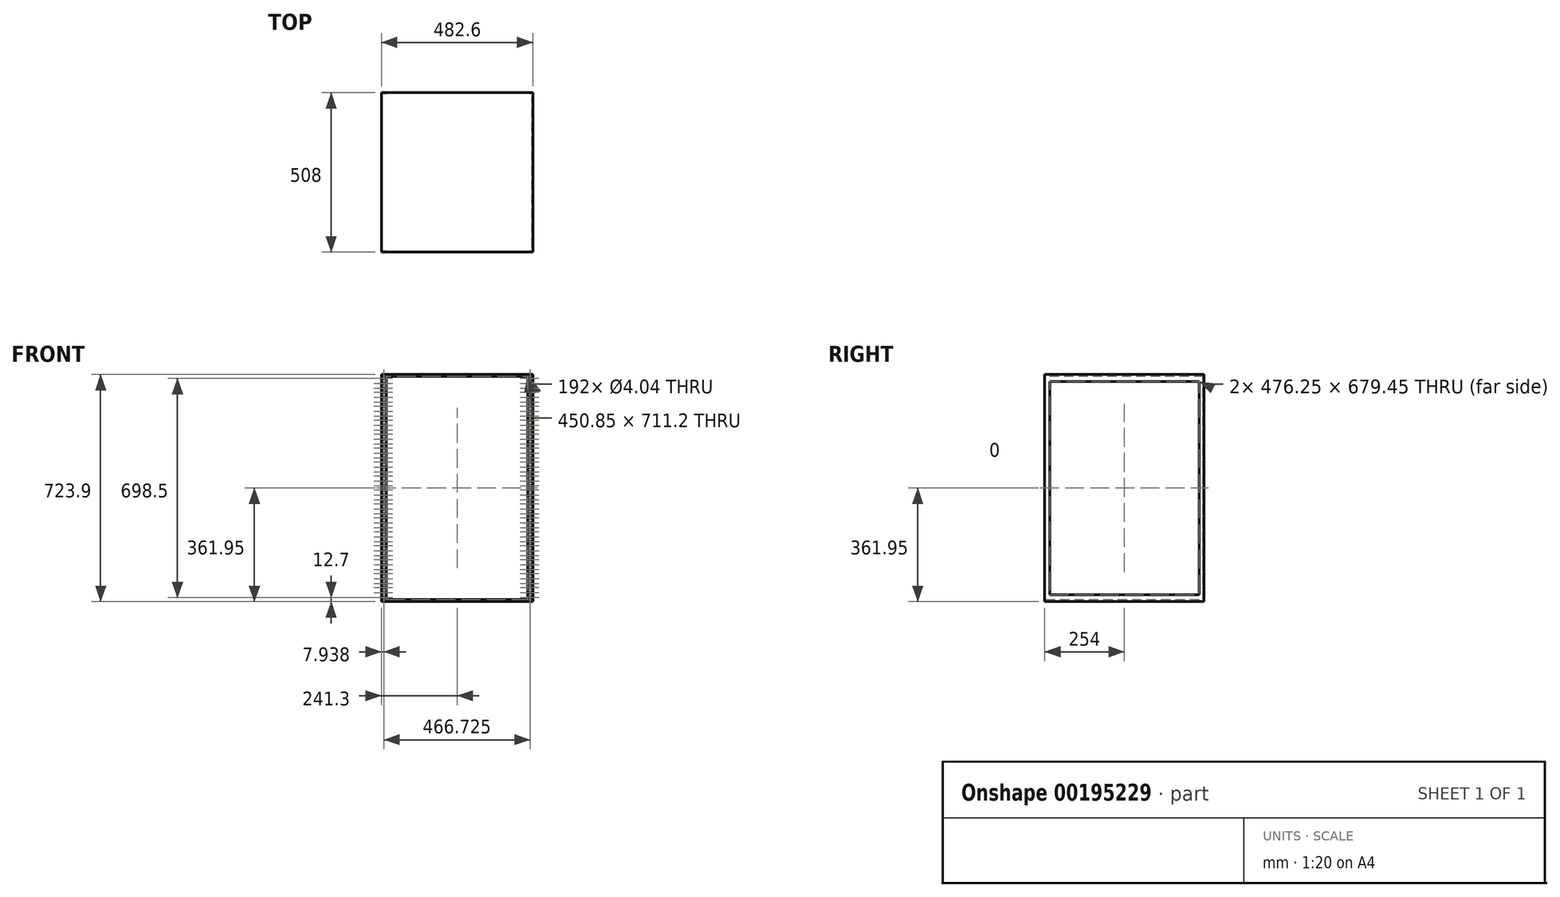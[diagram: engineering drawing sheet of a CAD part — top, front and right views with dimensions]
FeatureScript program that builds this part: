
annotation { "Feature Type Name" : "Feature", "Feature Type Description" : "" }
export const myFeature = defineFeature(function(context is Context, id is Id, definition is map)
    precondition{}
    {
        {
            var Q0;
            Q0=qCreatedBy(makeId("Front.planeOp"),FACE);
            var sketch = newSketch(context, id + "F0", { "sketchPlane" : qUnion([Q0])});
            skLineSegment(sketch, "E0.bottom", {"start": v(-241.3, 355.6) * mm, "end": v(241.3, 355.6) * mm});
            skLineSegment(sketch, "E0.top", {"start": v(-241.3, -355.6) * mm, "end": v(241.3, -355.6) * mm});
            skLineSegment(sketch, "E0.left", {"start": v(-241.3, 355.6) * mm, "end": v(-241.3, -355.6) * mm});
            skLineSegment(sketch, "E0.right", {"start": v(241.3, 355.6) * mm, "end": v(241.3, -355.6) * mm});
            skPoint(sketch, "E0.middle", {"position": v(0, 0) * mm});
            skSolve(sketch);
        }
        {
            var Q0;
            Q0 = qSketchRegion(id + "F0", true);
            extrude(context, id + "F1", {"entities" : qUnion([Q0]), "oppositeDirection" : true, "depth" : 508 * mm});
        }
        {
            var Q0;
            Q0=makeQuery(id+"F1.opExtrude","CAP_FACE",FACE,{"disambiguationData":[OSD([sQuery(id+"F0.wireOp",EDGE,"E0.bottom"),sQuery(id+"F0.wireOp",EDGE,"E0.top"),sQuery(id+"F0.wireOp",EDGE,"E0.left"),sQuery(id+"F0.wireOp",EDGE,"E0.right")])],"isStart":true});
            var sketch = newSketch(context, id + "F2", { "sketchPlane" : qUnion([Q0])});
            skLineSegment(sketch, "E1.bottom", {"start": v(-225.43, 355.6) * mm, "end": v(225.43, 355.6) * mm});
            skLineSegment(sketch, "E1.top", {"start": v(-225.43, -355.6) * mm, "end": v(225.43, -355.6) * mm});
            skLineSegment(sketch, "E1.left", {"start": v(-225.43, 355.6) * mm, "end": v(-225.43, -355.6) * mm});
            skLineSegment(sketch, "E1.right", {"start": v(225.43, 355.6) * mm, "end": v(225.43, -355.6) * mm});
            skPoint(sketch, "E1.middle", {"position": v(0, 0) * mm});
            skSolve(sketch);
        }
        {
            var Q0;
            Q0 = qSketchRegion(id + "F2", true);
            extrude(context, id + "F3", {"entities" : qUnion([Q0]), "operationType" : NewBodyOperationType.REMOVE, "endBound" : BoundingType.THROUGH_ALL, "oppositeDirection" : true, "depth" : 25.4 * mm});
        }
        {
            var Q0;
            Q0=makeQuery(id+"F1.opExtrude","SWEPT_FACE",FACE,{"disambiguationData":[OSD([sQuery(id+"F0.wireOp",EDGE,"E0.left")])]});
            var sketch = newSketch(context, id + "F4", { "sketchPlane" : qUnion([Q0])});
            skLineSegment(sketch, "E2.bottom", {"start": v(-492.13, 339.73) * mm, "end": v(-15.87, 339.73) * mm});
            skLineSegment(sketch, "E2.top", {"start": v(-492.13, -339.73) * mm, "end": v(-15.87, -339.73) * mm});
            skLineSegment(sketch, "E2.left", {"start": v(-492.13, 339.73) * mm, "end": v(-492.13, -339.73) * mm});
            skLineSegment(sketch, "E2.right", {"start": v(-15.88, 339.73) * mm, "end": v(-15.88, -339.73) * mm});
            skPoint(sketch, "E2.middle", {"position": v(-254, 0) * mm});
            skSolve(sketch);
        }
        {
            var Q0;
            Q0 = qSketchRegion(id + "F4", true);
            extrude(context, id + "F5", {"entities" : qUnion([Q0]), "operationType" : NewBodyOperationType.REMOVE, "endBound" : BoundingType.THROUGH_ALL, "oppositeDirection" : true, "depth" : 25.4 * mm});
        }
        {
            var Q0;
            Q0=makeQuery(id+"F1.opExtrude","SWEPT_FACE",FACE,{"disambiguationData":[OSD([sQuery(id+"F0.wireOp",EDGE,"E0.bottom")])]});
            var sketch = newSketch(context, id + "F6", { "sketchPlane" : qUnion([Q0])});
            skLineSegment(sketch, "E3.bottom", {"start": v(-238.76, 505.46) * mm, "end": v(238.76, 505.46) * mm});
            skLineSegment(sketch, "E3.top", {"start": v(-238.76, 2.54) * mm, "end": v(238.76, 2.54) * mm});
            skLineSegment(sketch, "E3.left", {"start": v(-238.76, 505.46) * mm, "end": v(-238.76, 2.54) * mm});
            skLineSegment(sketch, "E3.right", {"start": v(238.76, 505.46) * mm, "end": v(238.76, 2.54) * mm});
            skPoint(sketch, "E3.middle", {"position": v(0, 254) * mm});
            skSolve(sketch);
        }
        {
            var Q0;
            Q0 = qSketchRegion(id + "F6", true);
            extrude(context, id + "F7", {"entities" : qUnion([Q0]), "operationType" : NewBodyOperationType.REMOVE, "endBound" : BoundingType.THROUGH_ALL, "oppositeDirection" : true, "depth" : 25.4 * mm});
        }
        {
            var Q0;
            Q0=makeQuery(id+"F1.opExtrude","CAP_FACE",FACE,{"disambiguationData":[OSD([sQuery(id+"F0.wireOp",EDGE,"E0.bottom"),sQuery(id+"F0.wireOp",EDGE,"E0.top"),sQuery(id+"F0.wireOp",EDGE,"E0.left"),sQuery(id+"F0.wireOp",EDGE,"E0.right")])],"isStart":true});
            var sketch = newSketch(context, id + "F8", { "sketchPlane" : qUnion([Q0])});
            skPoint(sketch, "E4", {"position": v(-233.36, 349.25) * mm});
            skPoint(sketch, "E5", {"position": v(-233.36, 333.38) * mm});
            skPoint(sketch, "E6", {"position": v(-233.36, 317.5) * mm});
            skPoint(sketch, "E7.0.1.0", {"position": v(-233.36, 273.05) * mm});
            skPoint(sketch, "E7.0.1.1", {"position": v(-233.36, 288.93) * mm});
            skPoint(sketch, "E7.0.1.2", {"position": v(-233.36, 304.8) * mm});
            skPoint(sketch, "E7.0.2.0", {"position": v(-233.36, 228.6) * mm});
            skPoint(sketch, "E7.0.2.1", {"position": v(-233.36, 244.48) * mm});
            skPoint(sketch, "E7.0.2.2", {"position": v(-233.36, 260.35) * mm});
            skPoint(sketch, "E7.0.3.0", {"position": v(-233.36, 184.15) * mm});
            skPoint(sketch, "E7.0.3.1", {"position": v(-233.36, 200.03) * mm});
            skPoint(sketch, "E7.0.3.2", {"position": v(-233.36, 215.9) * mm});
            skPoint(sketch, "E7.0.4.0", {"position": v(-233.36, 139.7) * mm});
            skPoint(sketch, "E7.0.4.1", {"position": v(-233.36, 155.58) * mm});
            skPoint(sketch, "E7.0.4.2", {"position": v(-233.36, 171.45) * mm});
            skPoint(sketch, "E7.0.5.0", {"position": v(-233.36, 95.25) * mm});
            skPoint(sketch, "E7.0.5.1", {"position": v(-233.36, 111.13) * mm});
            skPoint(sketch, "E7.0.5.2", {"position": v(-233.36, 127) * mm});
            skPoint(sketch, "E7.0.6.0", {"position": v(-233.36, 50.8) * mm});
            skPoint(sketch, "E7.0.6.1", {"position": v(-233.36, 66.68) * mm});
            skPoint(sketch, "E7.0.6.2", {"position": v(-233.36, 82.55) * mm});
            skPoint(sketch, "E7.0.7.0", {"position": v(-233.36, 6.35) * mm});
            skPoint(sketch, "E7.0.7.1", {"position": v(-233.36, 22.23) * mm});
            skPoint(sketch, "E7.0.7.2", {"position": v(-233.36, 38.1) * mm});
            skPoint(sketch, "E7.0.8.0", {"position": v(-233.36, -38.1) * mm});
            skPoint(sketch, "E7.0.8.1", {"position": v(-233.36, -22.22) * mm});
            skPoint(sketch, "E7.0.8.2", {"position": v(-233.36, -6.35) * mm});
            skPoint(sketch, "E7.0.9.0", {"position": v(-233.36, -82.55) * mm});
            skPoint(sketch, "E7.0.9.1", {"position": v(-233.36, -66.67) * mm});
            skPoint(sketch, "E7.0.9.2", {"position": v(-233.36, -50.8) * mm});
            skPoint(sketch, "E7.0.10.0", {"position": v(-233.36, -127) * mm});
            skPoint(sketch, "E7.0.10.1", {"position": v(-233.36, -111.12) * mm});
            skPoint(sketch, "E7.0.10.2", {"position": v(-233.36, -95.25) * mm});
            skPoint(sketch, "E7.0.11.0", {"position": v(-233.36, -171.45) * mm});
            skPoint(sketch, "E7.0.11.1", {"position": v(-233.36, -155.57) * mm});
            skPoint(sketch, "E7.0.11.2", {"position": v(-233.36, -139.7) * mm});
            skPoint(sketch, "E7.0.12.0", {"position": v(-233.36, -215.9) * mm});
            skPoint(sketch, "E7.0.12.1", {"position": v(-233.36, -200.02) * mm});
            skPoint(sketch, "E7.0.12.2", {"position": v(-233.36, -184.15) * mm});
            skPoint(sketch, "E7.0.13.0", {"position": v(-233.36, -260.35) * mm});
            skPoint(sketch, "E7.0.13.1", {"position": v(-233.36, -244.47) * mm});
            skPoint(sketch, "E7.0.13.2", {"position": v(-233.36, -228.6) * mm});
            skPoint(sketch, "E7.0.14.0", {"position": v(-233.36, -304.8) * mm});
            skPoint(sketch, "E7.0.14.1", {"position": v(-233.36, -288.92) * mm});
            skPoint(sketch, "E7.0.14.2", {"position": v(-233.36, -273.05) * mm});
            skPoint(sketch, "E7.0.15.0", {"position": v(-233.36, -349.25) * mm});
            skPoint(sketch, "E7.0.15.1", {"position": v(-233.36, -333.37) * mm});
            skPoint(sketch, "E7.0.15.2", {"position": v(-233.36, -317.5) * mm});
            skLineSegment(sketch, "E7.direction1", {"start": v(-233.36, 317.5) * mm, "end": v(233.36, 317.5) * mm, "construction": true});
            skLineSegment(sketch, "E7.direction2", {"start": v(-233.36, 317.5) * mm, "end": v(-233.36, 273.05) * mm, "construction": true});
            skPoint(sketch, "E8.0.1.0", {"position": v(233.36, 317.5) * mm});
            skPoint(sketch, "E8.1.1.0", {"position": v(233.36, 333.38) * mm});
            skPoint(sketch, "E8.2.1.0", {"position": v(233.36, 349.25) * mm});
            skPoint(sketch, "E8.0.1.1", {"position": v(233.36, 273.05) * mm});
            skPoint(sketch, "E8.1.1.1", {"position": v(233.36, 288.93) * mm});
            skPoint(sketch, "E8.2.1.1", {"position": v(233.36, 304.8) * mm});
            skPoint(sketch, "E8.0.1.2", {"position": v(233.36, 228.6) * mm});
            skPoint(sketch, "E8.1.1.2", {"position": v(233.36, 244.48) * mm});
            skPoint(sketch, "E8.2.1.2", {"position": v(233.36, 260.35) * mm});
            skPoint(sketch, "E8.0.1.3", {"position": v(233.36, 184.15) * mm});
            skPoint(sketch, "E8.1.1.3", {"position": v(233.36, 200.03) * mm});
            skPoint(sketch, "E8.2.1.3", {"position": v(233.36, 215.9) * mm});
            skPoint(sketch, "E8.0.1.4", {"position": v(233.36, 139.7) * mm});
            skPoint(sketch, "E8.1.1.4", {"position": v(233.36, 155.58) * mm});
            skPoint(sketch, "E8.2.1.4", {"position": v(233.36, 171.45) * mm});
            skPoint(sketch, "E8.0.1.5", {"position": v(233.36, 95.25) * mm});
            skPoint(sketch, "E8.1.1.5", {"position": v(233.36, 111.13) * mm});
            skPoint(sketch, "E8.2.1.5", {"position": v(233.36, 127) * mm});
            skPoint(sketch, "E8.0.1.6", {"position": v(233.36, 50.8) * mm});
            skPoint(sketch, "E8.1.1.6", {"position": v(233.36, 66.68) * mm});
            skPoint(sketch, "E8.2.1.6", {"position": v(233.36, 82.55) * mm});
            skPoint(sketch, "E8.0.1.7", {"position": v(233.36, 6.35) * mm});
            skPoint(sketch, "E8.1.1.7", {"position": v(233.36, 22.23) * mm});
            skPoint(sketch, "E8.2.1.7", {"position": v(233.36, 38.1) * mm});
            skPoint(sketch, "E8.0.1.8", {"position": v(233.36, -38.1) * mm});
            skPoint(sketch, "E8.1.1.8", {"position": v(233.36, -22.22) * mm});
            skPoint(sketch, "E8.2.1.8", {"position": v(233.36, -6.35) * mm});
            skPoint(sketch, "E8.0.1.9", {"position": v(233.36, -82.55) * mm});
            skPoint(sketch, "E8.1.1.9", {"position": v(233.36, -66.67) * mm});
            skPoint(sketch, "E8.2.1.9", {"position": v(233.36, -50.8) * mm});
            skPoint(sketch, "E8.0.1.10", {"position": v(233.36, -127) * mm});
            skPoint(sketch, "E8.1.1.10", {"position": v(233.36, -111.12) * mm});
            skPoint(sketch, "E8.2.1.10", {"position": v(233.36, -95.25) * mm});
            skPoint(sketch, "E8.0.1.11", {"position": v(233.36, -171.45) * mm});
            skPoint(sketch, "E8.1.1.11", {"position": v(233.36, -155.57) * mm});
            skPoint(sketch, "E8.2.1.11", {"position": v(233.36, -139.7) * mm});
            skPoint(sketch, "E8.0.1.12", {"position": v(233.36, -215.9) * mm});
            skPoint(sketch, "E8.1.1.12", {"position": v(233.36, -200.02) * mm});
            skPoint(sketch, "E8.2.1.12", {"position": v(233.36, -184.15) * mm});
            skPoint(sketch, "E8.0.1.13", {"position": v(233.36, -260.35) * mm});
            skPoint(sketch, "E8.1.1.13", {"position": v(233.36, -244.47) * mm});
            skPoint(sketch, "E8.2.1.13", {"position": v(233.36, -228.6) * mm});
            skPoint(sketch, "E8.0.1.14", {"position": v(233.36, -304.8) * mm});
            skPoint(sketch, "E8.1.1.14", {"position": v(233.36, -288.92) * mm});
            skPoint(sketch, "E8.2.1.14", {"position": v(233.36, -273.05) * mm});
            skPoint(sketch, "E8.0.1.15", {"position": v(233.36, -349.25) * mm});
            skPoint(sketch, "E8.1.1.15", {"position": v(233.36, -333.37) * mm});
            skPoint(sketch, "E8.2.1.15", {"position": v(233.36, -317.5) * mm});
            skSolve(sketch);
        }
        {
            var Q0;
            Q0=sQuery(id+"F8.wireOp",VERTEX,"E7.0.2.2");
            var Q1;
            Q1=sQuery(id+"F8.wireOp",VERTEX,"E8.2.1.13");
            var Q2;
            Q2=sQuery(id+"F8.wireOp",VERTEX,"E8.2.1.10");
            var Q3;
            Q3=sQuery(id+"F8.wireOp",VERTEX,"E8.0.1.13");
            var Q4;
            Q4=sQuery(id+"F8.wireOp",VERTEX,"E8.1.1.2");
            var Q5;
            Q5=sQuery(id+"F8.wireOp",VERTEX,"E8.2.1.7");
            var Q6;
            Q6=sQuery(id+"F8.wireOp",VERTEX,"E8.1.1.3");
            var Q7;
            Q7=sQuery(id+"F8.wireOp",VERTEX,"E8.1.1.0");
            var Q8;
            Q8=sQuery(id+"F8.wireOp",VERTEX,"E8.2.1.5");
            var Q9;
            Q9=sQuery(id+"F8.wireOp",VERTEX,"E7.0.14.0");
            var Q10;
            Q10=sQuery(id+"F8.wireOp",VERTEX,"E7.0.11.0");
            var Q11;
            Q11=sQuery(id+"F8.wireOp",VERTEX,"E7.0.8.2");
            var Q12;
            Q12=sQuery(id+"F8.wireOp",VERTEX,"E7.0.5.2");
            var Q13;
            Q13=sQuery(id+"F8.wireOp",VERTEX,"E8.0.1.14");
            var Q14;
            Q14=sQuery(id+"F8.wireOp",VERTEX,"E7.0.8.0");
            var Q15;
            Q15=sQuery(id+"F8.wireOp",VERTEX,"E8.1.1.13");
            var Q16;
            Q16=sQuery(id+"F8.wireOp",VERTEX,"E8.0.1.8");
            var Q17;
            Q17=sQuery(id+"F8.wireOp",VERTEX,"E8.2.1.2");
            var Q18;
            Q18=sQuery(id+"F8.wireOp",VERTEX,"E8.0.1.6");
            var Q19;
            Q19=sQuery(id+"F8.wireOp",VERTEX,"E8.2.1.3");
            var Q20;
            Q20=sQuery(id+"F8.wireOp",VERTEX,"E8.2.1.0");
            var Q21;
            Q21=sQuery(id+"F8.wireOp",VERTEX,"E7.0.6.0");
            var Q22;
            Q22=sQuery(id+"F8.wireOp",VERTEX,"E7.0.11.1");
            var Q23;
            Q23=sQuery(id+"F8.wireOp",VERTEX,"E8.1.1.14");
            var Q24;
            Q24=sQuery(id+"F8.wireOp",VERTEX,"E8.1.1.11");
            var Q25;
            Q25=sQuery(id+"F8.wireOp",VERTEX,"E8.0.1.9");
            var Q26;
            Q26=sQuery(id+"F8.wireOp",VERTEX,"E7.0.11.2");
            var Q27;
            Q27=sQuery(id+"F8.wireOp",VERTEX,"E7.0.6.1");
            var Q28;
            Q28=sQuery(id+"F8.wireOp",VERTEX,"E8.2.1.11");
            var Q29;
            Q29=sQuery(id+"F8.wireOp",VERTEX,"E8.1.1.7");
            var Q30;
            Q30=sQuery(id+"F8.wireOp",VERTEX,"E8.0.1.5");
            var Q31;
            Q31=sQuery(id+"F8.wireOp",VERTEX,"E8.0.1.2");
            var Q32;
            Q32=sQuery(id+"F8.wireOp",VERTEX,"E7.0.15.2");
            var Q33;
            Q33=sQuery(id+"F8.wireOp",VERTEX,"E7.0.5.0");
            var Q34;
            Q34=sQuery(id+"F8.wireOp",VERTEX,"E7.0.10.1");
            var Q35;
            Q35=sQuery(id+"F8.wireOp",VERTEX,"E8.2.1.15");
            var Q36;
            Q36=sQuery(id+"F8.wireOp",VERTEX,"E7.0.3.0");
            var Q37;
            Q37=sQuery(id+"F8.wireOp",VERTEX,"E7.0.3.1");
            var Q38;
            Q38=sQuery(id+"F8.wireOp",VERTEX,"E8.1.1.10");
            var Q39;
            Q39=sQuery(id+"F8.wireOp",VERTEX,"E7.0.3.2");
            var Q40;
            Q40=sQuery(id+"F8.wireOp",VERTEX,"E7.direction1.end");
            var Q41;
            Q41=sQuery(id+"F8.wireOp",VERTEX,"E7.0.12.2");
            var Q42;
            Q42=sQuery(id+"F8.wireOp",VERTEX,"E7.0.7.1");
            var Q43;
            Q43=sQuery(id+"F8.wireOp",VERTEX,"E7.direction2.end");
            var Q44;
            Q44=sQuery(id+"F8.wireOp",VERTEX,"E4");
            var Q45;
            Q45=sQuery(id+"F8.wireOp",VERTEX,"E5");
            var Q46;
            Q46=sQuery(id+"F8.wireOp",VERTEX,"E8.0.1.11");
            var Q47;
            Q47=sQuery(id+"F8.wireOp",VERTEX,"E7.0.1.1");
            var Q48;
            Q48=sQuery(id+"F8.wireOp",VERTEX,"E7.0.13.2");
            var Q49;
            Q49=sQuery(id+"F8.wireOp",VERTEX,"E7.0.5.1");
            var Q50;
            Q50=sQuery(id+"F8.wireOp",VERTEX,"E8.1.1.8");
            var Q51;
            Q51=sQuery(id+"F8.wireOp",VERTEX,"E7.direction1.start");
            var Q52;
            Q52=sQuery(id+"F8.wireOp",VERTEX,"E8.1.1.6");
            var Q53;
            Q53=sQuery(id+"F8.wireOp",VERTEX,"E7.0.9.0");
            var Q54;
            Q54=sQuery(id+"F8.wireOp",VERTEX,"E7.0.14.1");
            var Q55;
            Q55=sQuery(id+"F8.wireOp",VERTEX,"E8.2.1.12");
            var Q56;
            Q56=sQuery(id+"F8.wireOp",VERTEX,"E8.0.1.3");
            var Q57;
            Q57=sQuery(id+"F8.wireOp",VERTEX,"E7.0.8.1");
            var Q58;
            Q58=sQuery(id+"F8.wireOp",VERTEX,"E7.0.10.2");
            var Q59;
            Q59=sQuery(id+"F8.wireOp",VERTEX,"E7.0.1.2");
            var Q60;
            Q60=sQuery(id+"F8.wireOp",VERTEX,"E7.0.2.1");
            var Q61;
            Q61=sQuery(id+"F8.wireOp",VERTEX,"E7.0.2.0");
            var Q62;
            Q62=sQuery(id+"F8.wireOp",VERTEX,"E7.0.7.2");
            var Q63;
            Q63=sQuery(id+"F8.wireOp",VERTEX,"E8.2.1.8");
            var Q64;
            Q64=sQuery(id+"F8.wireOp",VERTEX,"E7.0.13.1");
            var Q65;
            Q65=sQuery(id+"F8.wireOp",VERTEX,"E8.1.1.5");
            var Q66;
            Q66=sQuery(id+"F8.wireOp",VERTEX,"E7.0.14.2");
            var Q67;
            Q67=sQuery(id+"F8.wireOp",VERTEX,"E8.2.1.4");
            var Q68;
            Q68=sQuery(id+"F8.wireOp",VERTEX,"E8.2.1.1");
            var Q69;
            Q69=sQuery(id+"F8.wireOp",VERTEX,"E8.0.1.7");
            var Q70;
            Q70=sQuery(id+"F8.wireOp",VERTEX,"E8.1.1.12");
            var Q71;
            Q71=sQuery(id+"F8.wireOp",VERTEX,"E7.0.7.0");
            var Q72;
            Q72=sQuery(id+"F8.wireOp",VERTEX,"E7.0.12.1");
            var Q73;
            Q73=sQuery(id+"F8.wireOp",VERTEX,"E8.2.1.9");
            var Q74;
            Q74=sQuery(id+"F8.wireOp",VERTEX,"E8.0.1.15");
            var Q75;
            Q75=sQuery(id+"F8.wireOp",VERTEX,"E7.0.4.1");
            var Q76;
            Q76=sQuery(id+"F8.wireOp",VERTEX,"E7.0.9.2");
            var Q77;
            Q77=sQuery(id+"F8.wireOp",VERTEX,"E7.0.15.0");
            var Q78;
            Q78=sQuery(id+"F8.wireOp",VERTEX,"E8.1.1.4");
            var Q79;
            Q79=sQuery(id+"F8.wireOp",VERTEX,"E8.1.1.1");
            var Q80;
            Q80=sQuery(id+"F8.wireOp",VERTEX,"E8.2.1.6");
            var Q81;
            Q81=sQuery(id+"F8.wireOp",VERTEX,"E8.0.1.10");
            var Q82;
            Q82=sQuery(id+"F8.wireOp",VERTEX,"E8.1.1.15");
            var Q83;
            Q83=sQuery(id+"F8.wireOp",VERTEX,"E8.0.1.12");
            var Q84;
            Q84=sQuery(id+"F8.wireOp",VERTEX,"E7.0.6.2");
            var Q85;
            Q85=sQuery(id+"F8.wireOp",VERTEX,"E7.0.12.0");
            var Q86;
            Q86=sQuery(id+"F8.wireOp",VERTEX,"E8.1.1.9");
            var Q87;
            Q87=sQuery(id+"F8.wireOp",VERTEX,"E8.2.1.14");
            var Q88;
            Q88=sQuery(id+"F8.wireOp",VERTEX,"E7.0.4.2");
            var Q89;
            Q89=sQuery(id+"F8.wireOp",VERTEX,"E7.0.4.0");
            var Q90;
            Q90=sQuery(id+"F8.wireOp",VERTEX,"E7.0.9.1");
            var Q91;
            Q91=sQuery(id+"F8.wireOp",VERTEX,"E8.0.1.4");
            var Q92;
            Q92=sQuery(id+"F8.wireOp",VERTEX,"E8.0.1.1");
            var Q93;
            Q93=sQuery(id+"F8.wireOp",VERTEX,"E7.0.10.0");
            var Q94;
            Q94=sQuery(id+"F8.wireOp",VERTEX,"E7.0.15.1");
            var Q95;
            Q95=sQuery(id+"F8.wireOp",VERTEX,"E7.0.13.0");
            var Q96;
            Q96=makeQuery(id+"F3.boolean.opBoolean","SPLIT",BODY,{"disambiguationData":[OD(0.0)],"derivedFrom":makeQuery(id+"F1.opExtrude","SWEPT_BODY",BODY,{"disambiguationData":[OSD([sQuery(id+"F0.wireOp",EDGE,"E0.bottom"),sQuery(id+"F0.wireOp",EDGE,"E0.top"),sQuery(id+"F0.wireOp",EDGE,"E0.left"),sQuery(id+"F0.wireOp",EDGE,"E0.right")])]})});
            var Q97;
            Q97=makeQuery(id+"F3.boolean.opBoolean","SPLIT",BODY,{"disambiguationData":[OD(1.0)],"derivedFrom":makeQuery(id+"F1.opExtrude","SWEPT_BODY",BODY,{"disambiguationData":[OSD([sQuery(id+"F0.wireOp",EDGE,"E0.bottom"),sQuery(id+"F0.wireOp",EDGE,"E0.top"),sQuery(id+"F0.wireOp",EDGE,"E0.left"),sQuery(id+"F0.wireOp",EDGE,"E0.right")])]})});
            var Q98;
            Q98=makeQuery(id+"F3.boolean.opBoolean","SPLIT",BODY,{"disambiguationData":[OD(0.0)],"derivedFrom":makeQuery(id+"F1.opExtrude","SWEPT_BODY",BODY,{"disambiguationData":[OSD([sQuery(id+"F0.wireOp",EDGE,"E0.bottom"),sQuery(id+"F0.wireOp",EDGE,"E0.top"),sQuery(id+"F0.wireOp",EDGE,"E0.left"),sQuery(id+"F0.wireOp",EDGE,"E0.right")])]})});
            hole(context, id + "F9", {"style" : HoleStyle.SIMPLE, "endStyle" : HoleEndStyle.THROUGH, "standardTappedOrClearance" : lookupTablePath({ "standard" : "ANSI", "engagement" : "75%", "pitch" : "32 tpi", "size" : "#10", "type" : "Tapped" }), "standardBlindInLast" : lookupTablePath({ "standard" : "ANSI", "engagement" : "75%", "pitch" : "32 tpi", "size" : "#10", "type" : "Tapped" }), "holeDiameter" : 4.04 * mm, "locations" : qUnion([Q0, Q1, Q2, Q3, Q4, Q5, Q6, Q7, Q8, Q9, Q10, Q11, Q12, Q13, Q14, Q15, Q16, Q17, Q18, Q19, Q20, Q21, Q22, Q23, Q24, Q25, Q26, Q27, Q28, Q29, Q30, Q31, Q32, Q33, Q34, Q35, Q36, Q37, Q38, Q39, Q40, Q41, Q42, Q43, Q44, Q45, Q46, Q47, Q48, Q49, Q50, Q51, Q52, Q53, Q54, Q55, Q56, Q57, Q58, Q59, Q60, Q61, Q62, Q63, Q64, Q65, Q66, Q67, Q68, Q69, Q70, Q71, Q72, Q73, Q74, Q75, Q76, Q77, Q78, Q79, Q80, Q81, Q82, Q83, Q84, Q85, Q86, Q87, Q88, Q89, Q90, Q91, Q92, Q93, Q94, Q95]), "scope" : qUnion([Q96, Q97, Q98]), "isTappedThrough" : true, "majorDiameter" : 4.83 * mm, "showTappedDepth" : true});
        }
        {
            var Q0;
            {var subQ1=sQuery(id+"F0.wireOp",EDGE,"E0.left");var subQ3=sQuery(id+"F0.wireOp",EDGE,"E0.bottom");Q0=makeQuery(id+"F3.boolean.opBoolean","SPLIT",FACE,{"disambiguationData":[TD([makeQuery(id+"F1.opExtrude","SWEPT_FACE",FACE,{"disambiguationData":[OSD([subQ1])]})])],"derivedFrom":makeQuery(id+"F1.opExtrude","SWEPT_FACE",FACE,{"disambiguationData":[OSD([subQ3])]})});}
            var sketch = newSketch(context, id + "F10", { "sketchPlane" : qUnion([Q0])});
            skLineSegment(sketch, "E9.bottom", {"start": v(-241.3, 508) * mm, "end": v(241.3, 508) * mm});
            skLineSegment(sketch, "E9.top", {"start": v(-241.3, 0) * mm, "end": v(241.3, 0) * mm});
            skLineSegment(sketch, "E9.left", {"start": v(-241.3, 508) * mm, "end": v(-241.3, 0) * mm});
            skLineSegment(sketch, "E9.right", {"start": v(241.3, 508) * mm, "end": v(241.3, 0) * mm});
            skSolve(sketch);
        }
        {
            var Q0;
            Q0 = qSketchRegion(id + "F10", true);
            extrude(context, id + "F11", {"entities" : qUnion([Q0]), "operationType" : NewBodyOperationType.ADD, "depth" : 6.35 * mm});
        }
        {
            var Q0;
            {var subQ1=sQuery(id+"F0.wireOp",EDGE,"E0.left");var subQ2=sQuery(id+"F0.wireOp",EDGE,"E0.top");Q0=makeQuery(id+"F3.boolean.opBoolean","SPLIT",FACE,{"disambiguationData":[TD([makeQuery(id+"F1.opExtrude","SWEPT_FACE",FACE,{"disambiguationData":[OSD([subQ1])]})])],"derivedFrom":makeQuery(id+"F1.opExtrude","SWEPT_FACE",FACE,{"disambiguationData":[OSD([subQ2])]})});}
            var sketch = newSketch(context, id + "F12", { "sketchPlane" : qUnion([Q0])});
            skLineSegment(sketch, "E10.bottom", {"start": v(-241.3, 0) * mm, "end": v(241.3, 0) * mm});
            skLineSegment(sketch, "E10.top", {"start": v(-241.3, -508) * mm, "end": v(241.3, -508) * mm});
            skLineSegment(sketch, "E10.left", {"start": v(-241.3, 0) * mm, "end": v(-241.3, -508) * mm});
            skLineSegment(sketch, "E10.right", {"start": v(241.3, 0) * mm, "end": v(241.3, -508) * mm});
            skSolve(sketch);
        }
        {
            var Q0;
            Q0 = qSketchRegion(id + "F12", true);
            extrude(context, id + "F13", {"entities" : qUnion([Q0]), "operationType" : NewBodyOperationType.ADD, "depth" : 6.35 * mm});
        }
    });
